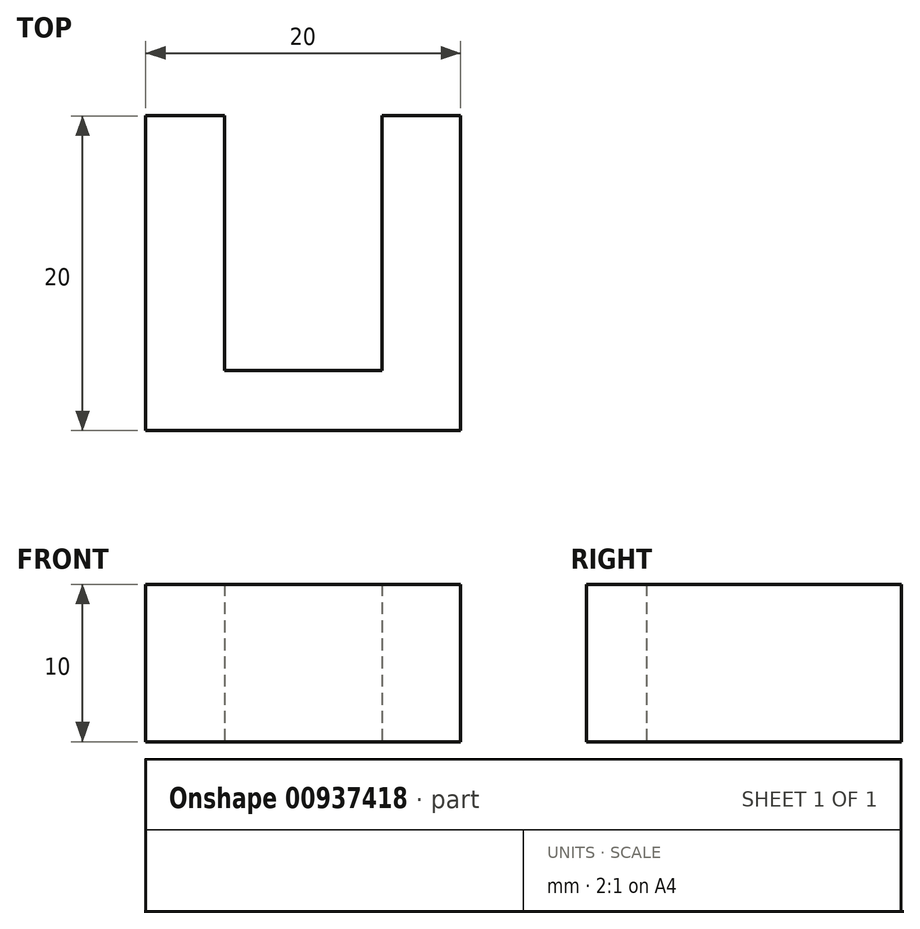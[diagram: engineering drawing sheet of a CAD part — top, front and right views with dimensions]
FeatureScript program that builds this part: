
annotation { "Feature Type Name" : "Feature", "Feature Type Description" : "" }
export const myFeature = defineFeature(function(context is Context, id is Id, definition is map)
    precondition{}
    {
        {
            var Q0;
            Q0=qCreatedBy(makeId("Top.planeOp"),FACE);
            var sketch = newSketch(context, id + "F0", { "sketchPlane" : qUnion([Q0])});
            skLineSegment(sketch, "E0", {"start": v(-37, 27.54) * mm, "end": v(-32, 27.54) * mm});
            skLineSegment(sketch, "E1", {"start": v(-32, 27.54) * mm, "end": v(-32, 11.36) * mm});
            skLineSegment(sketch, "E2", {"start": v(-32, 11.36) * mm, "end": v(-22, 11.36) * mm});
            skLineSegment(sketch, "E3", {"start": v(-22, 11.36) * mm, "end": v(-22, 27.54) * mm});
            skLineSegment(sketch, "E4", {"start": v(-22, 27.54) * mm, "end": v(-17, 27.54) * mm});
            skLineSegment(sketch, "E5", {"start": v(-17, 27.54) * mm, "end": v(-17, 7.54) * mm});
            skLineSegment(sketch, "E6", {"start": v(-17, 7.54) * mm, "end": v(-37, 7.54) * mm});
            skLineSegment(sketch, "E7", {"start": v(-37, 27.54) * mm, "end": v(-37, 7.54) * mm});
            skSolve(sketch);
        }
        {
            var Q0;
            Q0=makeQuery(id+"F0.imprint","IMPRINT",FACE,{"disambiguationData":[TD([[makeQuery(id+"F0.imprint","IMPRINT",EDGE,{"derivedFrom":sQuery(id+"F0.wireOp",EDGE,"E0")}),-1.0]])]});
            extrude(context, id + "F1", {"entities" : qUnion([Q0]), "depth" : 10 * mm, "offsetDistance" : 25 * mm});
        }
    });
